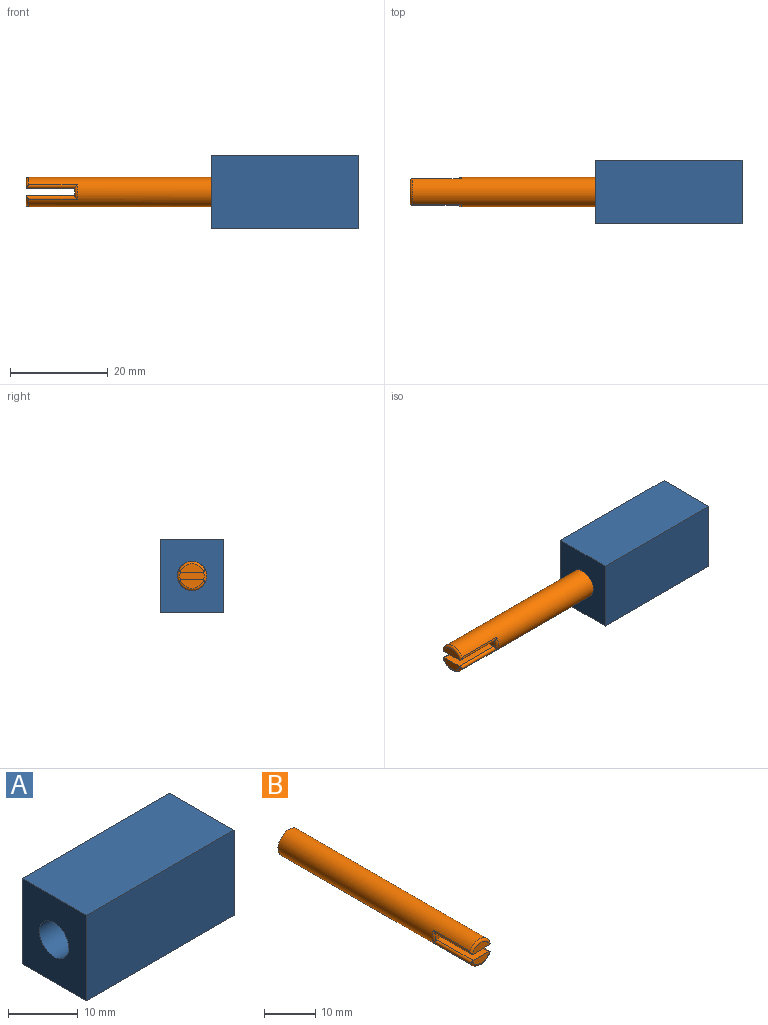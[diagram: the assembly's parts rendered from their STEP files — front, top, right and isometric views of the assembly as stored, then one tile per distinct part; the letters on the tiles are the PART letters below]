
ASSEMBLY  parts=2 mates=1
PART A: 8 faces, bbox 30x13x15 mm
  f0: plane 15x13mm, normal (1,0,0), area 195mm2, adj f1,f3,f4,f5
  f1: plane 30x13mm, normal (0,0,1), area 390mm2, adj f0,f2,f4,f5
  f2: plane 15x13mm, normal (-1,0,0), area 166.7mm2, adj f1,f3,f4,f5,f7
  f3: plane 30x13mm, normal (0,0,-1), area 390mm2, adj f0,f2,f4,f5
  f4: plane 30x15mm, normal (0,-1,0), area 450mm2, adj f0,f1,f2,f3
  f5: plane 30x15mm, normal (0,1,0), area 450mm2, adj f0,f1,f2,f3
  f6: cone r=0mm half-angle=59deg, axis (-1,0,0), area 33mm2, adj f7
  f7: cylinder r=3mm len=25mm, axis (-1,0,0), area 471.2mm2, adj f2,f6
PART B: 15 faces, bbox 6.5x53x6.5 mm
  f0: plane 4.74x1.75mm, normal (0,-1,0), area 6.1mm2, adj f5,f12,f13,f14
  f1: cylinder r=3mm len=52.5mm, axis (0,1,0), area 926.8mm2, adj f3,f7,f8,f9,f10,f11,f12,f13
  f2: plane 4.74x1.75mm, normal (0,-1,0), area 6.1mm2, adj f4,f7,f8,f9
  f3: plane 6x6mm, normal (0,1,0), area 28.3mm2, adj f1
  f4: plane 10x4.33mm, normal (0,0,-1), area 43.3mm2, adj f2,f6,f8,f9
  f5: plane 10x4.33mm, normal (0,0,1), area 43.3mm2, adj f0,f6,f12,f13
  f6: plane 5x1.59mm, normal (0,-1,0), area 7.4mm2, adj f4,f5,f8,f9,f10,f11,f12,f13
  f7: torus R=2.5mm, axis (0,-1,0), area 5.2mm2, adj f1,f2,f8,f9
  f8: cylinder r=0.5mm len=10.5mm, axis (0,1,0), area 10.5mm2, adj f1,f2,f4,f6,f7,f10
  f9: cylinder r=0.5mm len=10.5mm, axis (0,1,0), area 10.5mm2, adj f1,f2,f4,f6,f7,f11
  f10: torus R=2.5mm, axis (0,-1,0), area 1.8mm2, adj f1,f6,f8,f12
  f11: torus R=2.5mm, axis (0,-1,0), area 1.8mm2, adj f1,f6,f9,f13
  f12: cylinder r=0.5mm len=10.5mm, axis (0,1,0), area 10.5mm2, adj f0,f1,f5,f6,f10,f14
  f13: cylinder r=0.5mm len=10.5mm, axis (0,1,0), area 10.5mm2, adj f0,f1,f5,f6,f11,f14
  f14: torus R=2.5mm, axis (0,-1,0), area 5.2mm2, adj f0,f1,f12,f13
PLACE A at identity fixed
PLACE B rot(axis=(0,0,-1),90deg) t=(-26.5,0,0)mm
MATE cylindrical A.f7 <-> B.f1  axis (-1,0,0) through (-15,0,0)mm
